# Revit family: NO TRIM SLIDER
name_source: partatom
category: Windows
units: mm (PartAtom-declared; Revit-internal decimal feet)

## family parameters
Always vertical = Yes
Cut with Voids When Loaded = No
Host = Wall
OmniClass Number = 23.30.20.17.21.14
OmniClass Title = Casement Windows
Room Calculation Point = No
Shared = No

## types (1)
- 48" x 48"
    Analytic Construction = 1/8 in Pilkington single glazing
    Assembly Code = B2020100
    Construction Type Id = GSP4R
    Default Sill Height = 3' - 0"
    Define Thermal Properties by = Schematic Type
    Glass Pane Material = Glass
    Heat Transfer Coefficient (U) = 0.6496 BTU/(h·ft²·°F)
    Height = 4' - 0"
    HeightFeet = 4
    HeightInches = 0
    HeightReal = 4
    Manufacturer = ALPINE
    Model = A272
    Sash Material = Metal - Black Matte
    Solar Heat Gain Coefficient = 0.78
    Thermal Resistance (R) = 1.5394 (h·ft²·°F)/BTU
    Trim Exterior Material = Wood - Matte Black
    Trim Interior Material = Wood - Matte Black
    Trim Projection - Ext. = 0' - 0 1/2"
    Trim Projection - Int. = 0' - 0 3/4"
    Trim Width - Exterior = 0' - 5 1/2"
    Trim Width - Interior = 0' - 3 1/2"
    Visual Light Transmittance = 0.9
    Wall Closure = By host
    Width = 4' - 0"
    WidthFeet = 4
    WidthInches = 0
    WidthReal = 4
    Window Inset = 0' - 0 3/4"

## geometry (parser evidence)
native form markers: Sweep x1
no freeform markers — native parametric forms only
